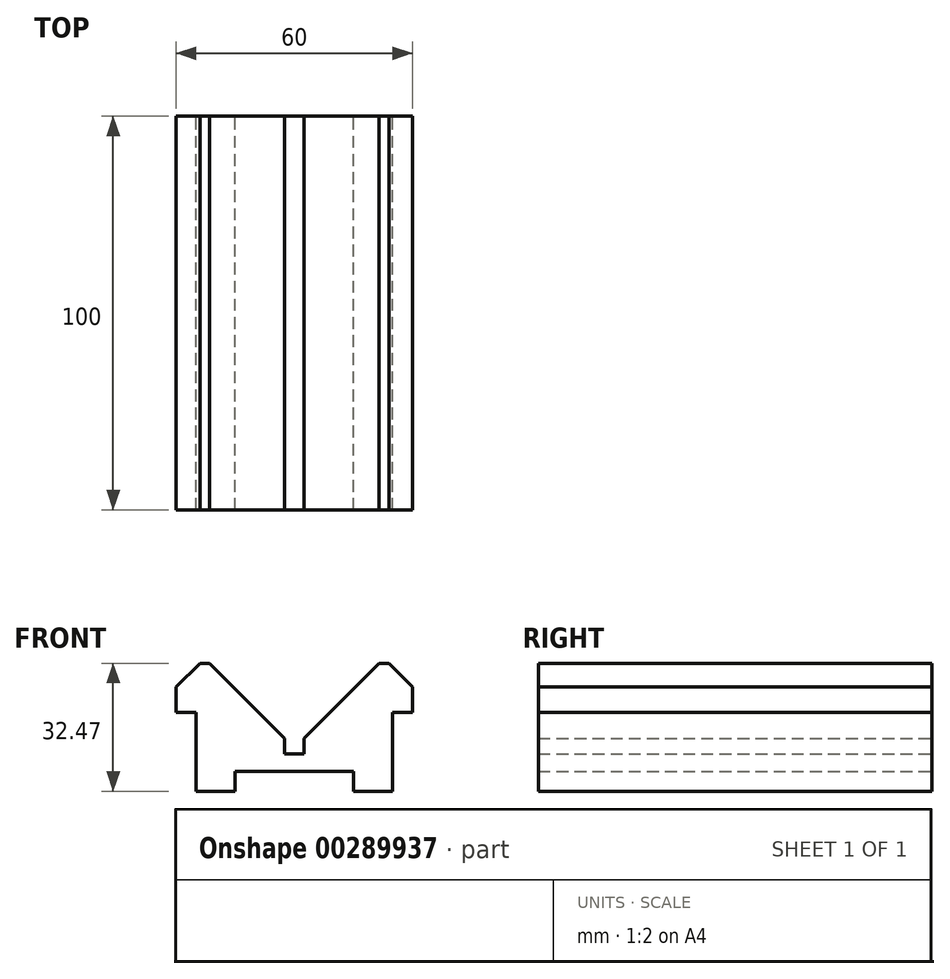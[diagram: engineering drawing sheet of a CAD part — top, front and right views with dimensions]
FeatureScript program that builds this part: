
annotation { "Feature Type Name" : "Feature", "Feature Type Description" : "" }
export const myFeature = defineFeature(function(context is Context, id is Id, definition is map)
    precondition{}
    {
        {
            var Q0;
            Q0=qCreatedBy(makeId("Front.planeOp"),FACE);
            var sketch = newSketch(context, id + "F0", { "sketchPlane" : qUnion([Q0])});
            skLineSegment(sketch, "E0", {"start": v(-2.5, 11.4) * mm, "end": v(-2.5, 15.4) * mm});
            skLineSegment(sketch, "E1", {"start": v(-2.5, 15.4) * mm, "end": v(-21.5, 34.4) * mm});
            skLineSegment(sketch, "E2", {"start": v(-21.5, 34.4) * mm, "end": v(-24, 34.4) * mm});
            skLineSegment(sketch, "E3", {"start": v(-24, 34.4) * mm, "end": v(-30, 28.4) * mm});
            skLineSegment(sketch, "E4", {"start": v(-30, 28.4) * mm, "end": v(-30, 21.93) * mm});
            skLineSegment(sketch, "E5", {"start": v(-30, 21.93) * mm, "end": v(-25, 21.93) * mm});
            skLineSegment(sketch, "E6", {"start": v(-25, 21.93) * mm, "end": v(-25, 1.93) * mm});
            skLineSegment(sketch, "E7", {"start": v(-25, 1.93) * mm, "end": v(-15, 1.93) * mm});
            skLineSegment(sketch, "E8", {"start": v(-15, 1.93) * mm, "end": v(-15, 6.93) * mm});
            skLineSegment(sketch, "E9", {"start": v(0, 45.72) * mm, "end": v(0, -28.29) * mm, "construction": true});
            skLineSegment(sketch, "E10.MirrorCS", {"start": v(2.5, 11.4) * mm, "end": v(2.5, 15.4) * mm});
            skLineSegment(sketch, "E11.MirrorCS", {"start": v(2.5, 15.4) * mm, "end": v(21.5, 34.4) * mm});
            skLineSegment(sketch, "E12.MirrorCS", {"start": v(21.5, 34.4) * mm, "end": v(24, 34.4) * mm});
            skLineSegment(sketch, "E13.MirrorCS", {"start": v(24, 34.4) * mm, "end": v(30, 28.4) * mm});
            skLineSegment(sketch, "E14.MirrorCS", {"start": v(30, 28.4) * mm, "end": v(30, 21.93) * mm});
            skLineSegment(sketch, "E15.MirrorCS", {"start": v(30, 21.93) * mm, "end": v(25, 21.93) * mm});
            skLineSegment(sketch, "E16.MirrorCS", {"start": v(25, 21.93) * mm, "end": v(25, 1.93) * mm});
            skLineSegment(sketch, "E17.MirrorCS", {"start": v(25, 1.93) * mm, "end": v(15, 1.93) * mm});
            skLineSegment(sketch, "E18.MirrorCS", {"start": v(15, 1.93) * mm, "end": v(15, 6.93) * mm});
            skPoint(sketch, "E19.start.orphan", {"position": v(0, 11.77) * mm});
            skLineSegment(sketch, "E20", {"start": v(-2.5, 11.4) * mm, "end": v(2.5, 11.4) * mm});
            skPoint(sketch, "E21.end.orphan", {"position": v(0, 6.93) * mm});
            skPoint(sketch, "E22.MirrorCS.start.orphan", {"position": v(15, 6.93) * mm});
            skLineSegment(sketch, "E23", {"start": v(-15, 6.93) * mm, "end": v(15, 6.93) * mm});
            skSolve(sketch);
        }
        {
            var Q0;
            Q0=makeQuery(id+"F0.imprint","IMPRINT",FACE,{"disambiguationData":[TD([[makeQuery(id+"F0.imprint","IMPRINT",EDGE,{"derivedFrom":sQuery(id+"F0.wireOp",EDGE,"E0")}),1.0]])]});
            extrude(context, id + "F1", {"entities" : qUnion([Q0]), "depth" : 100 * mm});
        }
    });
